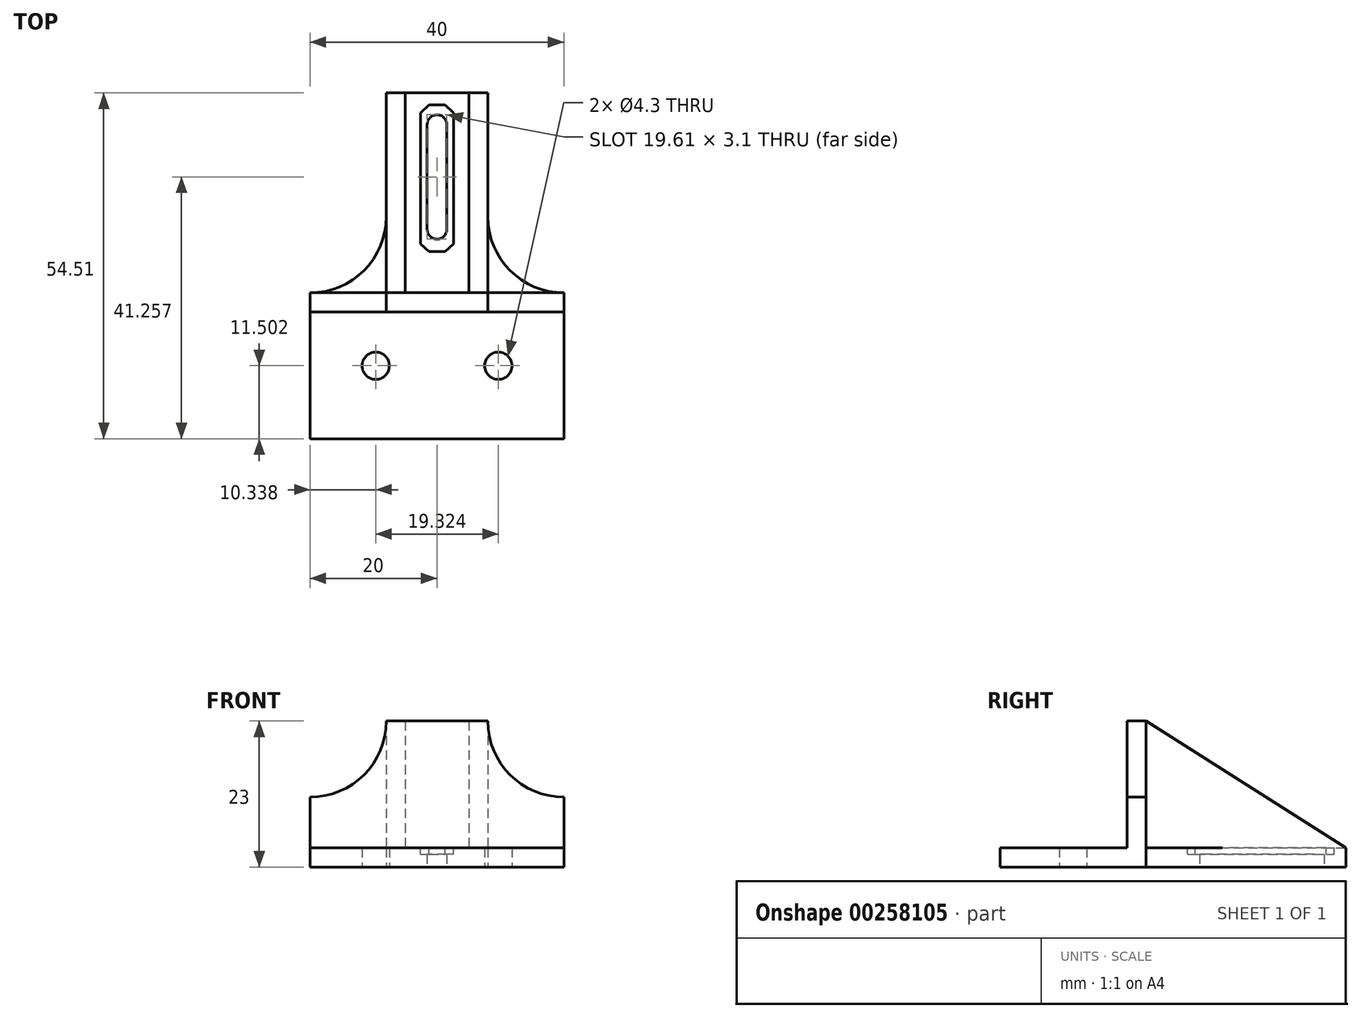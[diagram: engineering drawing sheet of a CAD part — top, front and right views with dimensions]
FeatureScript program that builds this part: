
annotation { "Feature Type Name" : "Feature", "Feature Type Description" : "" }
export const myFeature = defineFeature(function(context is Context, id is Id, definition is map)
    precondition{}
    {
        {
            var Q0;
            Q0=qCreatedBy(makeId("Top.planeOp"),FACE);
            var sketch = newSketch(context, id + "F0", { "sketchPlane" : qUnion([Q0])});
            skLineSegment(sketch, "E0.bottom", {"start": v(-20, -7.72) * mm, "end": v(20, -7.72) * mm});
            skLineSegment(sketch, "E0.top", {"start": v(-20, -30.72) * mm, "end": v(20, -30.72) * mm});
            skLineSegment(sketch, "E0.left", {"start": v(-20, -7.72) * mm, "end": v(-20, -30.72) * mm});
            skLineSegment(sketch, "E0.right", {"start": v(20, -7.72) * mm, "end": v(20, -30.72) * mm});
            skPoint(sketch, "E0.middle", {"position": v(0, -19.22) * mm});
            skLineSegment(sketch, "E1.bottom", {"start": v(-8, 23.8) * mm, "end": v(8, 23.8) * mm});
            skLineSegment(sketch, "E1.top", {"start": v(-8, -7.72) * mm, "end": v(8, -7.72) * mm});
            skLineSegment(sketch, "E1.left", {"start": v(-8, 23.8) * mm, "end": v(-8, -7.72) * mm});
            skLineSegment(sketch, "E1.right", {"start": v(8, 23.8) * mm, "end": v(8, -7.72) * mm});
            skPoint(sketch, "E1.middle", {"position": v(0, 8.04) * mm});
            skArc(sketch, "E2", {"start": v(-20, -7.72) * mm, "mid": v(-11.51, -4.2) * mm, "end": v(-8, 4.28) * mm});
            skArc(sketch, "E3", {"start": v(8, 4.28) * mm, "mid": v(11.51, -4.2) * mm, "end": v(20, -7.72) * mm});
            skCircle(sketch, "E4", {"center": v(-9.66, -19.22) * mm, "radius": 2.15 * mm});
            skCircle(sketch, "E5", {"center": v(9.66, -19.22) * mm, "radius": 2.15 * mm});
            skCircle(sketch, "E6", {"center": v(0, 18.8) * mm, "radius": 1.55 * mm});
            skCircle(sketch, "E7", {"center": v(0, 2.28) * mm, "radius": 1.55 * mm});
            skLineSegment(sketch, "E8", {"start": v(-1.55, 18.8) * mm, "end": v(-1.55, 2.28) * mm});
            skLineSegment(sketch, "E9", {"start": v(1.55, 18.8) * mm, "end": v(1.55, 2.28) * mm});
            skSolve(sketch);
        }
        {
            var Q0;
            {var subQ4=sQuery(id+"F0.wireOp",EDGE,"E1.bottom");Q0=makeQuery(id+"F0.imprint","IMPRINT",FACE,{"disambiguationData":[TD([[makeQuery(id+"F0.imprint","IMPRINT",EDGE,{"derivedFrom":subQ4}),-1.0]])]});}
            var Q1;
            {var subQ0=sQuery(id+"F0.wireOp",EDGE,"E2");Q1=makeQuery(id+"F0.imprint","IMPRINT",FACE,{"disambiguationData":[TD([[makeQuery(id+"F0.imprint","IMPRINT",EDGE,{"derivedFrom":subQ0}),-1.0]])]});}
            var Q2;
            {var subQ0=sQuery(id+"F0.wireOp",EDGE,"E3");Q2=makeQuery(id+"F0.imprint","IMPRINT",FACE,{"disambiguationData":[TD([[makeQuery(id+"F0.imprint","IMPRINT",EDGE,{"derivedFrom":subQ0}),-1.0]])]});}
            var Q3;
            Q3=makeQuery(id+"F0.imprint","IMPRINT",FACE,{"disambiguationData":[TD([[makeQuery(id+"F0.imprint","IMPRINT",EDGE,{"derivedFrom":sQuery(id+"F0.wireOp",EDGE,"E0.top")}),1.0]])]});
            extrude(context, id + "F1", {"entities" : qUnion([Q0, Q1, Q2, Q3]), "depth" : 3 * mm});
        }
        {
            var Q0;
            Q0=makeQuery(id+"F1.opExtrude","CAP_FACE",FACE,{"disambiguationData":[OSD([sQuery(id+"F0.wireOp",EDGE,"E0.top"),sQuery(id+"F0.wireOp",EDGE,"E0.left"),sQuery(id+"F0.wireOp",EDGE,"E0.right"),sQuery(id+"F0.wireOp",EDGE,"E1.bottom"),sQuery(id+"F0.wireOp",EDGE,"E1.left"),sQuery(id+"F0.wireOp",EDGE,"E1.right"),sQuery(id+"F0.wireOp",EDGE,"E2"),sQuery(id+"F0.wireOp",EDGE,"E3")])],"isStart":false});
            var sketch = newSketch(context, id + "F2", { "sketchPlane" : qUnion([Q0])});
            skLineSegment(sketch, "E10.bottom", {"start": v(-20, -7.72) * mm, "end": v(20, -7.72) * mm});
            skLineSegment(sketch, "E10.top", {"start": v(-20, -10.72) * mm, "end": v(20, -10.72) * mm});
            skLineSegment(sketch, "E10.left", {"start": v(-20, -7.72) * mm, "end": v(-20, -10.72) * mm});
            skLineSegment(sketch, "E10.right", {"start": v(20, -7.72) * mm, "end": v(20, -10.72) * mm});
            skSolve(sketch);
        }
        {
            var Q0;
            Q0=makeQuery(id+"F2.imprint","IMPRINT",FACE,{"disambiguationData":[TD([[makeQuery(id+"F2.imprint","IMPRINT",EDGE,{"derivedFrom":sQuery(id+"F2.wireOp",EDGE,"E10.bottom")}),-1.0]])]});
            extrude(context, id + "F3", {"entities" : qUnion([Q0]), "operationType" : NewBodyOperationType.ADD, "depth" : 20 * mm});
        }
        {
            var Q0;
            Q0=makeQuery(id+"F3.opExtrude","SWEPT_FACE",FACE,{"disambiguationData":[OSD([sQuery(id+"F2.wireOp",EDGE,"E10.top")])]});
            var sketch = newSketch(context, id + "F4", { "sketchPlane" : qUnion([Q0])});
            skArc(sketch, "E11", {"start": v(-20, 11) * mm, "mid": v(-11.51, 14.51) * mm, "end": v(-8, 23) * mm});
            skArc(sketch, "E12", {"start": v(8, 23) * mm, "mid": v(11.51, 14.51) * mm, "end": v(20, 11) * mm});
            skSolve(sketch);
        }
        {
            var Q0;
            {var subQ0=sQuery(id+"F4.wireOp",EDGE,"E11");Q0=makeQuery(id+"F4.imprint","IMPRINT",FACE,{"disambiguationData":[TD([[makeQuery(id+"F4.imprint","IMPRINT",EDGE,{"derivedFrom":subQ0}),1.0]])]});}
            var Q1;
            {var subQ0=sQuery(id+"F4.wireOp",EDGE,"E12");Q1=makeQuery(id+"F4.imprint","IMPRINT",FACE,{"disambiguationData":[TD([[makeQuery(id+"F4.imprint","IMPRINT",EDGE,{"derivedFrom":subQ0}),1.0]])]});}
            extrude(context, id + "F5", {"entities" : qUnion([Q0, Q1]), "operationType" : NewBodyOperationType.REMOVE, "oppositeDirection" : true, "depth" : 4 * mm});
        }
        {
            var Q0;
            Q0=makeQuery(id+"F3.boolean.opBoolean","MERGE",FACE,{"derivedFrom":[makeQuery(id+"F1.opExtrude","SWEPT_FACE",FACE,{"disambiguationData":[OSD([sQuery(id+"F0.wireOp",EDGE,"E0.right")])]}),makeQuery(id+"F3.opExtrude","SWEPT_FACE",FACE,{"disambiguationData":[OSD([sQuery(id+"F2.wireOp",EDGE,"E10.right")])]})]});
            var sketch = newSketch(context, id + "F6", { "sketchPlane" : qUnion([Q0])});
            skLineSegment(sketch, "E13", {"start": v(-7.72, 23) * mm, "end": v(-7.72, 3) * mm});
            skLineSegment(sketch, "E14", {"start": v(-7.72, 3) * mm, "end": v(23.8, 3) * mm});
            skLineSegment(sketch, "E15", {"start": v(-7.72, 23) * mm, "end": v(23.8, 3) * mm});
            skSolve(sketch);
        }
        {
            var Q0;
            {var subQ4=sQuery(id+"F6.wireOp",EDGE,"E14");Q0=makeQuery(id+"F6.imprint","IMPRINT",FACE,{"disambiguationData":[TD([[makeQuery(id+"F6.imprint","IMPRINT",EDGE,{"derivedFrom":subQ4}),1.0]])]});}
            extrude(context, id + "F7", {"entities" : qUnion([Q0]), "operationType" : NewBodyOperationType.ADD, "oppositeDirection" : true, "depth" : 15 * mm, "hasSecondDirection" : true, "secondDirectionOppositeDirection" : true, "secondDirectionDepth" : 12 * mm});
        }
        {
            var Q0;
            Q0 = qSketchRegion(id + "F6", true);
            extrude(context, id + "F8", {"entities" : qUnion([Q0]), "operationType" : NewBodyOperationType.ADD, "oppositeDirection" : true, "depth" : 28 * mm, "hasSecondDirection" : true, "secondDirectionOppositeDirection" : true, "secondDirectionDepth" : 25 * mm});
        }
        {
            var Q0;
            {var subQ0=sQuery(id+"F0.wireOp",EDGE,"E8");var subQ2=sQuery(id+"F0.wireOp",EDGE,"E7");var subQ4=sQuery(id+"F0.wireOp",EDGE,"E6");var subQ6=sQuery(id+"F0.wireOp",EDGE,"E1.bottom");var subQ7=makeQuery(id+"F1.opExtrude","SWEPT_FACE",FACE,{"disambiguationData":[OSD([subQ6])]});var subQ9=sQuery(id+"F0.wireOp",EDGE,"E9");var subQ17=sQuery(id+"F0.wireOp",EDGE,"E0.left");var subQ18=makeQuery(id+"F1.opExtrude","SWEPT_FACE",FACE,{"disambiguationData":[OSD([subQ17])]});var subQ19=sQuery(id+"F0.wireOp",EDGE,"E2");var subQ21=sQuery(id+"F0.wireOp",EDGE,"E1.left");var subQ23=sQuery(id+"F0.wireOp",EDGE,"E3");var subQ24=sQuery(id+"F0.wireOp",EDGE,"E1.right");var subQ25=sQuery(id+"F0.wireOp",EDGE,"E0.right");Q0=makeQuery(id+"F8.boolean.opBoolean","SPLIT",FACE,{"disambiguationData":[TD([subQ7])],"derivedFrom":makeQuery(id+"F7.boolean.opBoolean","SPLIT",FACE,{"disambiguationData":[TD([subQ18])],"derivedFrom":makeQuery(id+"F3.boolean.opBoolean","SPLIT",FACE,{"disambiguationData":[TD([subQ7])],"derivedFrom":makeQuery(id+"F1.opExtrude","CAP_FACE",FACE,{"disambiguationData":[OSD([sQuery(id+"F0.wireOp",EDGE,"E0.top"),subQ17,subQ25,subQ6,subQ21,subQ24,subQ19,subQ23,sQuery(id+"F0.wireOp",EDGE,"E4"),sQuery(id+"F0.wireOp",EDGE,"E5"),subQ4,subQ2,subQ0,subQ9])],"isStart":false})})})});}
            var sketch = newSketch(context, id + "F9", { "sketchPlane" : qUnion([Q0])});
            skLineSegment(sketch, "E16", {"start": v(-1.25, 21.9) * mm, "end": v(1.25, 21.9) * mm});
            skLineSegment(sketch, "E17", {"start": v(1.25, 21.9) * mm, "end": v(2.6, 20.65) * mm});
            skLineSegment(sketch, "E18", {"start": v(2.6, 20.65) * mm, "end": v(2.6, 0) * mm});
            skLineSegment(sketch, "E19", {"start": v(2.6, 0) * mm, "end": v(1.25, -1.2) * mm});
            skLineSegment(sketch, "E20", {"start": v(1.25, -1.2) * mm, "end": v(-1.25, -1.2) * mm});
            skLineSegment(sketch, "E21", {"start": v(-1.25, -1.2) * mm, "end": v(-2.6, 0) * mm});
            skLineSegment(sketch, "E22", {"start": v(-2.6, 0) * mm, "end": v(-2.6, 20.65) * mm});
            skLineSegment(sketch, "E23", {"start": v(-2.6, 20.65) * mm, "end": v(-1.25, 21.9) * mm});
            skSolve(sketch);
        }
        {
            var Q0;
            Q0=makeQuery(id+"F9.imprint","IMPRINT",FACE,{"disambiguationData":[TD([[makeQuery(id+"F9.imprint","IMPRINT",EDGE,{"derivedFrom":sQuery(id+"F9.wireOp",EDGE,"E16")}),-1.0]])]});
            extrude(context, id + "F10", {"entities" : qUnion([Q0]), "operationType" : NewBodyOperationType.REMOVE, "oppositeDirection" : true, "depth" : 1 * mm});
        }
    });
